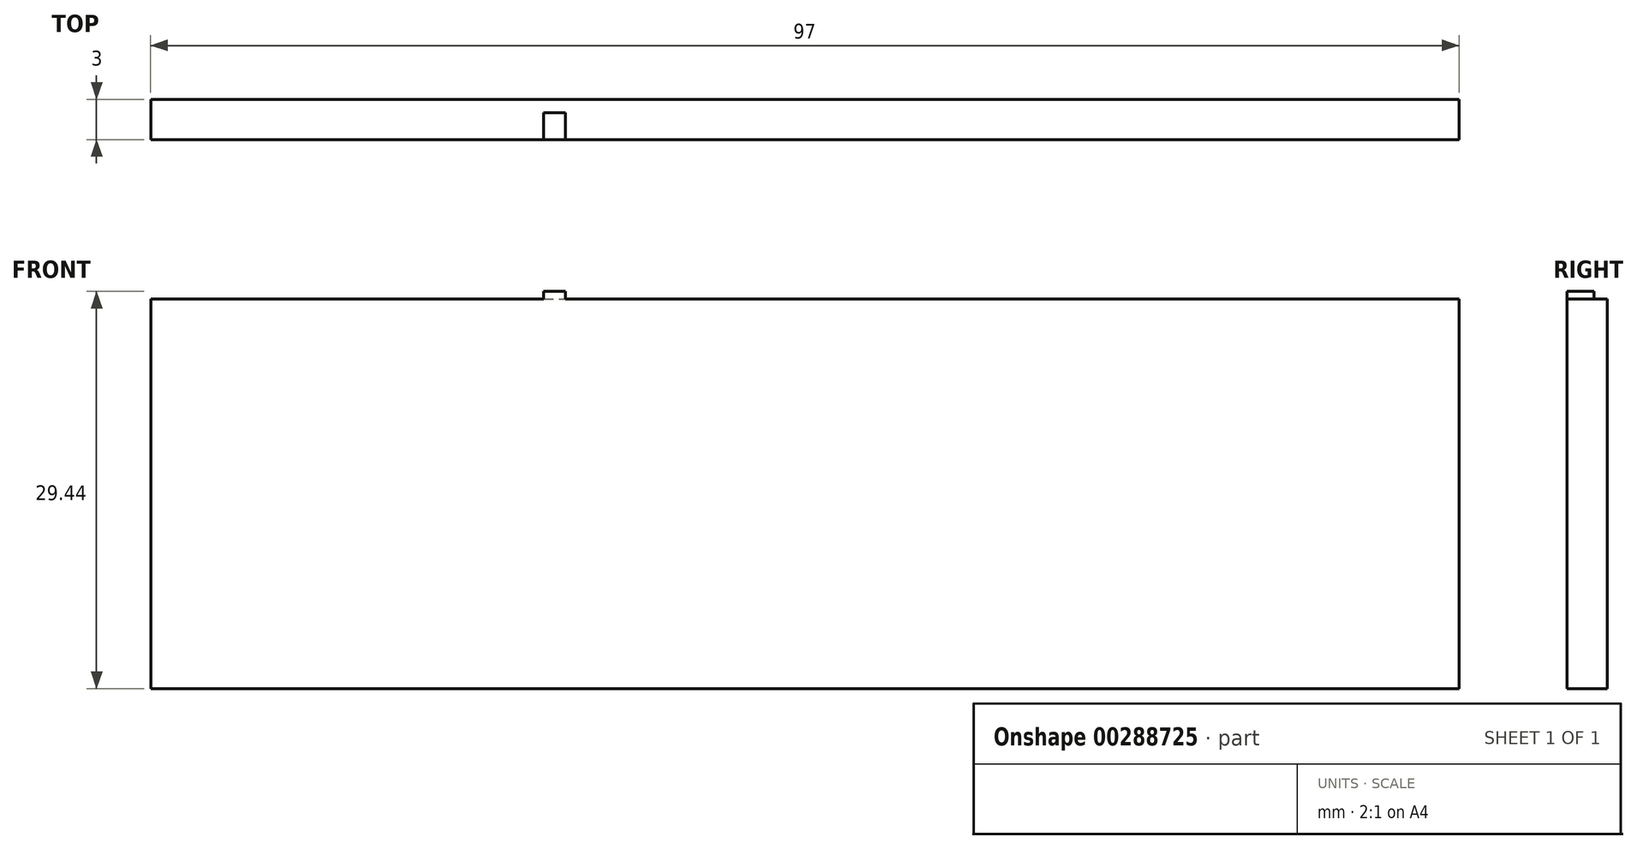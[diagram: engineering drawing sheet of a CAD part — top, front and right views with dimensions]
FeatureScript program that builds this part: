
annotation { "Feature Type Name" : "Feature", "Feature Type Description" : "" }
export const myFeature = defineFeature(function(context is Context, id is Id, definition is map)
    precondition{}
    {
        {
            var Q0;
            Q0=qCreatedBy(makeId("Front.planeOp"),FACE);
            var sketch = newSketch(context, id + "F0", { "sketchPlane" : qUnion([Q0])});
            skLineSegment(sketch, "E0.bottom", {"start": v(-55.33, 33.02) * mm, "end": v(41.67, 33.02) * mm});
            skLineSegment(sketch, "E0.top", {"start": v(-55.33, 4.15) * mm, "end": v(41.67, 4.15) * mm});
            skLineSegment(sketch, "E0.left", {"start": v(-55.33, 33.02) * mm, "end": v(-55.33, 4.15) * mm});
            skLineSegment(sketch, "E0.right", {"start": v(41.67, 33.02) * mm, "end": v(41.67, 4.15) * mm});
            skSolve(sketch);
        }
        {
            var Q0;
            Q0 = qSketchRegion(id + "F0", true);
            extrude(context, id + "F1", {"entities" : qUnion([Q0]), "depth" : 3 * mm});
        }
        {
            var Q0;
            Q0=makeQuery(id+"F1.opExtrude","CAP_FACE",FACE,{"disambiguationData":[OSD([sQuery(id+"F0.wireOp",EDGE,"E0.bottom"),sQuery(id+"F0.wireOp",EDGE,"E0.top"),sQuery(id+"F0.wireOp",EDGE,"E0.left"),sQuery(id+"F0.wireOp",EDGE,"E0.right")])],"isStart":false});
            var sketch = newSketch(context, id + "F2", { "sketchPlane" : qUnion([Q0])});
            skText(sketch, "E1", { "text": "3rd PLACE", "fontName": "OpenSans-Regular.ttf"});
            const initialGuessF2  = {"E1": [-0.0546, 0.01846, 1, 0, 0.01434]};
            skSetInitialGuess(sketch, initialGuessF2);
            skSolve(sketch);
        }
        {
            var Q0;
            Q0 = qSketchRegion(id + "F2", true);
            extrude(context, id + "F3", {"entities" : qUnion([Q0]), "operationType" : NewBodyOperationType.ADD, "oppositeDirection" : true, "depth" : 2 * mm});
        }
    });
